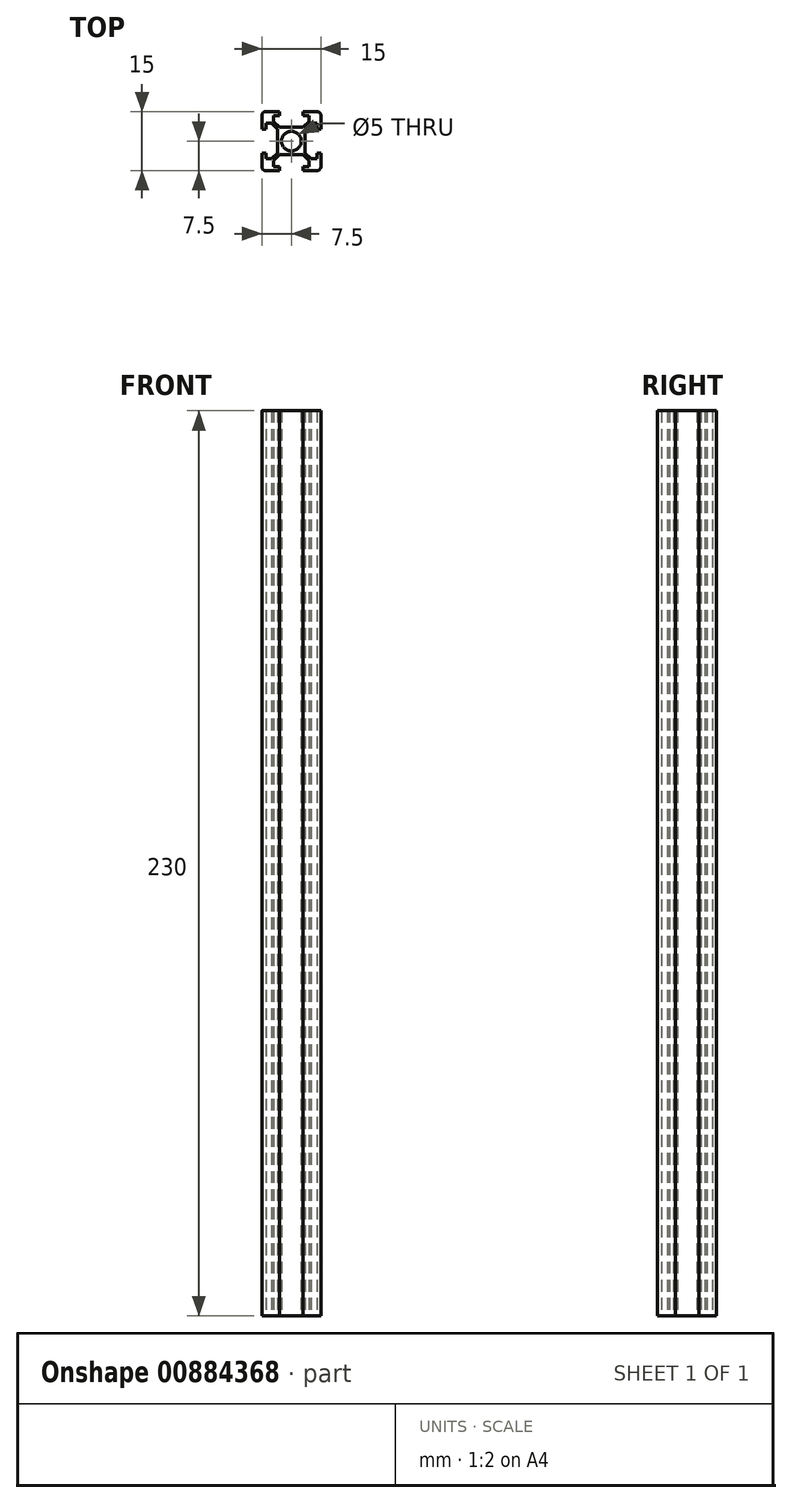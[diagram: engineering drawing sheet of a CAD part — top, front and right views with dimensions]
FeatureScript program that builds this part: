
annotation { "Feature Type Name" : "Feature", "Feature Type Description" : "" }
export const myFeature = defineFeature(function(context is Context, id is Id, definition is map)
    precondition{}
    {
        {
            var Q0;
            Q0=qCreatedBy(makeId("Top.planeOp"),FACE);
            var sketch = newSketch(context, id + "F0", { "sketchPlane" : qUnion([Q0])});
            skCircle(sketch, "E0", {"center": v(0, 0) * mm, "radius": 2.5 * mm});
            skLineSegment(sketch, "E1.bottom", {"start": v(6.5, 7.5) * mm, "end": v(3, 7.5) * mm});
            skLineSegment(sketch, "E1.top", {"start": v(6.5, -7.5) * mm, "end": v(3, -7.5) * mm});
            skLineSegment(sketch, "E1.left", {"start": v(7.5, 6.5) * mm, "end": v(7.5, 3) * mm});
            skLineSegment(sketch, "E1.right", {"start": v(-7.5, 6.5) * mm, "end": v(-7.5, 3) * mm});
            skPoint(sketch, "E2.visualSharp", {"position": v(-7.5, 7.5) * mm});
            skArc(sketch, "E2.filletArc", {"start": v(-6.5, 7.5) * mm, "mid": v(-7.2, 7.2) * mm, "end": v(-7.5, 6.5) * mm});
            skPoint(sketch, "E3.visualSharp", {"position": v(7.5, 7.5) * mm});
            skArc(sketch, "E3.filletArc", {"start": v(7.5, 6.5) * mm, "mid": v(7.2, 7.2) * mm, "end": v(6.5, 7.5) * mm});
            skPoint(sketch, "E4.visualSharp", {"position": v(7.5, -7.5) * mm});
            skArc(sketch, "E4.filletArc", {"start": v(6.5, -7.5) * mm, "mid": v(7.2, -7.2) * mm, "end": v(7.5, -6.5) * mm});
            skPoint(sketch, "E5.visualSharp", {"position": v(-7.5, -7.5) * mm});
            skArc(sketch, "E5.filletArc", {"start": v(-7.5, -6.5) * mm, "mid": v(-7.2, -7.2) * mm, "end": v(-6.5, -7.5) * mm});
            skLineSegment(sketch, "E6", {"start": v(-3, 7.5) * mm, "end": v(-3, 6.5) * mm});
            skLineSegment(sketch, "E7", {"start": v(3, 7.5) * mm, "end": v(3, 6.5) * mm});
            skLineSegment(sketch, "E8", {"start": v(-4.5, 6.5) * mm, "end": v(-4.5, 5) * mm});
            skLineSegment(sketch, "E9", {"start": v(4.5, 5) * mm, "end": v(4.5, 6.5) * mm});
            skLineSegment(sketch, "E10", {"start": v(4.5, 6.5) * mm, "end": v(3, 6.5) * mm});
            skLineSegment(sketch, "E11", {"start": v(-3, 3.5) * mm, "end": v(3, 3.5) * mm});
            skLineSegment(sketch, "E12", {"start": v(3, 3.5) * mm, "end": v(4.5, 5) * mm});
            skLineSegment(sketch, "E13", {"start": v(-3, 3.5) * mm, "end": v(-4.5, 5) * mm});
            skLineSegment(sketch, "E14.trimOffspring", {"start": v(-3, 6.5) * mm, "end": v(-4.5, 6.5) * mm});
            skLineSegment(sketch, "E15", {"start": v(-3, -7.5) * mm, "end": v(-3, -6.5) * mm});
            skLineSegment(sketch, "E16", {"start": v(-3, -6.5) * mm, "end": v(-4.5, -6.5) * mm});
            skLineSegment(sketch, "E17", {"start": v(-4.5, -6.5) * mm, "end": v(-4.5, -5) * mm});
            skLineSegment(sketch, "E18", {"start": v(-4.5, -5) * mm, "end": v(-3, -3.5) * mm});
            skLineSegment(sketch, "E19", {"start": v(-3, -3.5) * mm, "end": v(3, -3.5) * mm});
            skLineSegment(sketch, "E20", {"start": v(3, -3.5) * mm, "end": v(4.5, -5) * mm});
            skLineSegment(sketch, "E21", {"start": v(4.5, -5) * mm, "end": v(4.5, -6.5) * mm});
            skLineSegment(sketch, "E22", {"start": v(4.5, -6.5) * mm, "end": v(3, -6.5) * mm});
            skLineSegment(sketch, "E23", {"start": v(3, -6.5) * mm, "end": v(3, -7.5) * mm});
            skPoint(sketch, "E24", {"position": v(0, 7.5) * mm});
            skPoint(sketch, "E25", {"position": v(0, -7.5) * mm});
            skPoint(sketch, "E26", {"position": v(7.5, 0) * mm});
            skPoint(sketch, "E27", {"position": v(-7.5, 0) * mm});
            skLineSegment(sketch, "E28", {"start": v(7.5, 3) * mm, "end": v(6.5, 3) * mm});
            skLineSegment(sketch, "E29", {"start": v(6.5, 3) * mm, "end": v(6.5, 4.5) * mm});
            skLineSegment(sketch, "E30", {"start": v(6.5, 4.5) * mm, "end": v(5, 4.5) * mm});
            skLineSegment(sketch, "E31", {"start": v(5, 4.5) * mm, "end": v(3.5, 3) * mm});
            skLineSegment(sketch, "E32", {"start": v(3.5, 3) * mm, "end": v(3.5, -3) * mm});
            skLineSegment(sketch, "E33", {"start": v(3.5, -3) * mm, "end": v(5, -4.5) * mm});
            skLineSegment(sketch, "E34", {"start": v(5, -4.5) * mm, "end": v(6.5, -4.5) * mm});
            skLineSegment(sketch, "E35", {"start": v(6.5, -4.5) * mm, "end": v(6.5, -3) * mm});
            skLineSegment(sketch, "E36", {"start": v(6.5, -3) * mm, "end": v(7.5, -3) * mm});
            skLineSegment(sketch, "E37.trimOffspring", {"start": v(-3, 7.5) * mm, "end": v(-6.5, 7.5) * mm});
            skLineSegment(sketch, "E38.trimOffspring", {"start": v(7.5, -3) * mm, "end": v(7.5, -6.5) * mm});
            skLineSegment(sketch, "E39.trimOffspring", {"start": v(-3, -7.5) * mm, "end": v(-6.5, -7.5) * mm});
            skLineSegment(sketch, "E40", {"start": v(-7.5, 3) * mm, "end": v(-6.5, 3) * mm});
            skLineSegment(sketch, "E41", {"start": v(-6.5, 3) * mm, "end": v(-6.5, 4.5) * mm});
            skLineSegment(sketch, "E42", {"start": v(-6.5, 4.5) * mm, "end": v(-5, 4.5) * mm});
            skLineSegment(sketch, "E43", {"start": v(-5, 4.5) * mm, "end": v(-3.5, 3) * mm});
            skLineSegment(sketch, "E44", {"start": v(-3.5, 3) * mm, "end": v(-3.5, -3) * mm});
            skLineSegment(sketch, "E45", {"start": v(-3.5, -3) * mm, "end": v(-5, -4.5) * mm});
            skLineSegment(sketch, "E46", {"start": v(-5, -4.5) * mm, "end": v(-6.5, -4.5) * mm});
            skLineSegment(sketch, "E47", {"start": v(-6.5, -4.5) * mm, "end": v(-6.5, -3) * mm});
            skLineSegment(sketch, "E48", {"start": v(-6.5, -3) * mm, "end": v(-7.5, -3) * mm});
            skLineSegment(sketch, "E49.trimOffspring", {"start": v(-7.5, -3) * mm, "end": v(-7.5, -6.5) * mm});
            skSolve(sketch);
        }
        {
            var Q0;
            Q0 = qSketchRegion(id + "F0", true);
            extrude(context, id + "F1", {"entities" : qUnion([Q0]), "depth" : 230 * mm, "offsetDistance" : 25 * mm});
        }
    });
